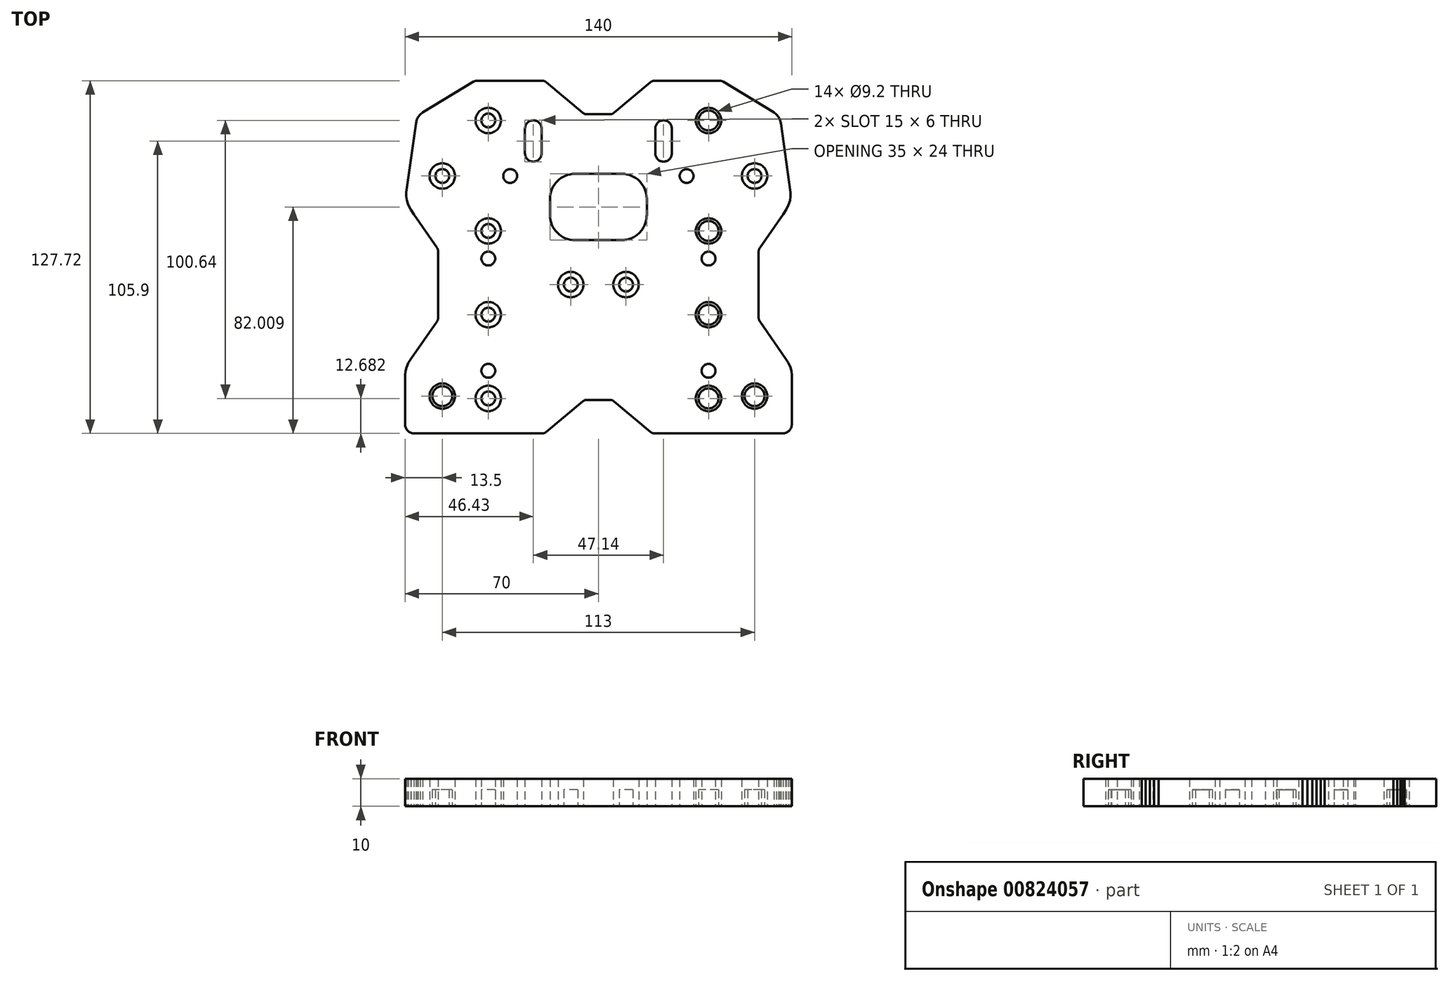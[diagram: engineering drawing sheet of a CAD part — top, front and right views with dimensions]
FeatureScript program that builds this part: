
annotation { "Feature Type Name" : "Feature", "Feature Type Description" : "" }
export const myFeature = defineFeature(function(context is Context, id is Id, definition is map)
    precondition{}
    {
        {
            var Q0;
            Q0=qCreatedBy(makeId("Top.planeOp"),FACE);
            var sketch = newSketch(context, id + "F0", { "sketchPlane" : qUnion([Q0])});
            skLineSegment(sketch, "E0", {"start": v(-63.59, 52.34) * mm, "end": v(-64.5, 51.65) * mm});
            skLineSegment(sketch, "E1", {"start": v(-64.5, 51.65) * mm, "end": v(-65.2, 50.76) * mm});
            skLineSegment(sketch, "E2", {"start": v(-65.2, 50.76) * mm, "end": v(-65.7, 49.68) * mm});
            skLineSegment(sketch, "E3", {"start": v(-65.7, 49.68) * mm, "end": v(-66.02, 48.35) * mm});
            skLineSegment(sketch, "E4", {"start": v(-63.59, 52.34) * mm, "end": v(-45.13, 63.52) * mm});
            skLineSegment(sketch, "E5", {"start": v(-70, -42.75) * mm, "end": v(-70, -60.5) * mm});
            skLineSegment(sketch, "E6", {"start": v(-69.52, 23.45) * mm, "end": v(-66.02, 48.35) * mm});
            skLineSegment(sketch, "E7", {"start": v(-70, -42.75) * mm, "end": v(-69.87, -41.37) * mm});
            skLineSegment(sketch, "E8", {"start": v(-69.87, -41.37) * mm, "end": v(-69.45, -39.88) * mm});
            skLineSegment(sketch, "E9", {"start": v(-69.45, -39.88) * mm, "end": v(-68.74, -38.32) * mm});
            skLineSegment(sketch, "E10", {"start": v(-68.74, -38.32) * mm, "end": v(-67.73, -36.7) * mm});
            skLineSegment(sketch, "E11", {"start": v(-66.64, -63.86) * mm, "end": v(-20.35, -63.86) * mm});
            skLineSegment(sketch, "E12", {"start": v(20.35, -63.86) * mm, "end": v(66.64, -63.86) * mm});
            skLineSegment(sketch, "E13", {"start": v(-58, -22) * mm, "end": v(-58, 2.08) * mm});
            skLineSegment(sketch, "E14", {"start": v(4.14, -51.7) * mm, "end": v(-4.14, -51.7) * mm});
            skLineSegment(sketch, "E15", {"start": v(-58.43, 3.42) * mm, "end": v(-66.79, 15.4) * mm});
            skLineSegment(sketch, "E16", {"start": v(-66.79, 15.4) * mm, "end": v(-67.92, 17.2) * mm});
            skLineSegment(sketch, "E17", {"start": v(-67.92, 17.2) * mm, "end": v(-68.77, 18.92) * mm});
            skLineSegment(sketch, "E18", {"start": v(-68.77, 18.92) * mm, "end": v(-69.32, 20.55) * mm});
            skLineSegment(sketch, "E19", {"start": v(-69.32, 20.55) * mm, "end": v(-69.57, 22.07) * mm});
            skLineSegment(sketch, "E20", {"start": v(-69.57, 22.07) * mm, "end": v(-69.52, 23.45) * mm});
            skLineSegment(sketch, "E21", {"start": v(-67.73, -36.7) * mm, "end": v(-58.43, -23.34) * mm});
            skLineSegment(sketch, "E22", {"start": v(5.66, 52.25) * mm, "end": v(18.84, 63.31) * mm});
            skLineSegment(sketch, "E23", {"start": v(18.84, -63.31) * mm, "end": v(5.66, -52.25) * mm});
            skLineSegment(sketch, "E24", {"start": v(-26.57, 46.54) * mm, "end": v(-26.57, 37.54) * mm});
            skLineSegment(sketch, "E25", {"start": v(-20.57, 37.54) * mm, "end": v(-20.57, 46.54) * mm});
            skLineSegment(sketch, "E26", {"start": v(-17.5, 21.1) * mm, "end": v(-17.5, 15.2) * mm});
            skLineSegment(sketch, "E27", {"start": v(-8.45, 6.15) * mm, "end": v(8.45, 6.15) * mm});
            skLineSegment(sketch, "E28", {"start": v(17.5, 15.2) * mm, "end": v(17.5, 21.1) * mm});
            skLineSegment(sketch, "E29", {"start": v(20.57, 46.54) * mm, "end": v(20.57, 37.54) * mm});
            skLineSegment(sketch, "E30", {"start": v(26.57, 37.54) * mm, "end": v(26.57, 46.54) * mm});
            skLineSegment(sketch, "E31", {"start": v(8.45, 30.15) * mm, "end": v(-8.45, 30.15) * mm});
            skLineSegment(sketch, "E32", {"start": v(-5.66, -52.25) * mm, "end": v(-18.84, -63.31) * mm});
            skLineSegment(sketch, "E33", {"start": v(-18.84, 63.31) * mm, "end": v(-5.66, 52.25) * mm});
            skLineSegment(sketch, "E34", {"start": v(58.43, -23.33) * mm, "end": v(67.73, -36.7) * mm});
            skLineSegment(sketch, "E35", {"start": v(66.78, 15.4) * mm, "end": v(58.43, 3.42) * mm});
            skLineSegment(sketch, "E36", {"start": v(-4.14, 51.7) * mm, "end": v(4.14, 51.7) * mm});
            skLineSegment(sketch, "E37", {"start": v(58, 2.08) * mm, "end": v(58, -22) * mm});
            skLineSegment(sketch, "E38", {"start": v(43.91, 63.86) * mm, "end": v(20.35, 63.86) * mm});
            skLineSegment(sketch, "E39", {"start": v(-20.35, 63.86) * mm, "end": v(-43.91, 63.86) * mm});
            skLineSegment(sketch, "E40", {"start": v(70, -42.75) * mm, "end": v(69.87, -41.37) * mm});
            skLineSegment(sketch, "E41", {"start": v(69.87, -41.37) * mm, "end": v(69.45, -39.88) * mm});
            skLineSegment(sketch, "E42", {"start": v(69.45, -39.88) * mm, "end": v(68.74, -38.32) * mm});
            skLineSegment(sketch, "E43", {"start": v(68.74, -38.32) * mm, "end": v(67.73, -36.7) * mm});
            skLineSegment(sketch, "E44", {"start": v(69.52, 23.45) * mm, "end": v(69.57, 22.07) * mm});
            skLineSegment(sketch, "E45", {"start": v(69.57, 22.07) * mm, "end": v(69.32, 20.55) * mm});
            skLineSegment(sketch, "E46", {"start": v(69.32, 20.55) * mm, "end": v(68.77, 18.92) * mm});
            skLineSegment(sketch, "E47", {"start": v(68.77, 18.92) * mm, "end": v(67.92, 17.2) * mm});
            skLineSegment(sketch, "E48", {"start": v(67.92, 17.2) * mm, "end": v(66.78, 15.4) * mm});
            skLineSegment(sketch, "E49", {"start": v(70, -60.5) * mm, "end": v(70, -42.75) * mm});
            skLineSegment(sketch, "E50", {"start": v(66.02, 48.35) * mm, "end": v(65.7, 49.7) * mm});
            skLineSegment(sketch, "E51", {"start": v(65.7, 49.7) * mm, "end": v(65.17, 50.8) * mm});
            skLineSegment(sketch, "E52", {"start": v(65.17, 50.8) * mm, "end": v(64.47, 51.66) * mm});
            skLineSegment(sketch, "E53", {"start": v(64.47, 51.66) * mm, "end": v(63.59, 52.34) * mm});
            skLineSegment(sketch, "E54", {"start": v(66.02, 48.35) * mm, "end": v(69.52, 23.45) * mm});
            skLineSegment(sketch, "E55", {"start": v(45.13, 63.52) * mm, "end": v(63.59, 52.34) * mm});
            skCircle(sketch, "E56", {"center": v(-56.5, -50.34) * mm, "radius": 3.6 * mm});
            skArc(sketch, "E57", {"start": v(-70, -60.5) * mm, "mid": v(-69.02, -62.88) * mm, "end": v(-66.64, -63.86) * mm});
            skCircle(sketch, "E58", {"center": v(-10, -9.96) * mm, "radius": 2.5 * mm});
            skCircle(sketch, "E59", {"center": v(-39.85, -51.18) * mm, "radius": 2.5 * mm});
            skCircle(sketch, "E60", {"center": v(-39.85, -41.18) * mm, "radius": 2.5 * mm});
            skCircle(sketch, "E61", {"center": v(-39.85, -20.86) * mm, "radius": 2.5 * mm});
            skCircle(sketch, "E62", {"center": v(-39.85, -0.54) * mm, "radius": 2.5 * mm});
            skArc(sketch, "E63", {"start": v(-4.14, -51.7) * mm, "mid": v(-4.95, -51.84) * mm, "end": v(-5.66, -52.25) * mm});
            skArc(sketch, "E64", {"start": v(-58.43, -23.34) * mm, "mid": v(-58.11, -22.7) * mm, "end": v(-58, -22) * mm});
            skArc(sketch, "E65", {"start": v(-20.35, -63.86) * mm, "mid": v(-19.54, -63.72) * mm, "end": v(-18.84, -63.31) * mm});
            skArc(sketch, "E66", {"start": v(-8.45, 30.15) * mm, "mid": v(-14.85, 27.5) * mm, "end": v(-17.5, 21.1) * mm});
            skArc(sketch, "E67", {"start": v(-17.5, 15.2) * mm, "mid": v(-14.85, 8.8) * mm, "end": v(-8.45, 6.15) * mm});
            skArc(sketch, "E68", {"start": v(-20.57, 46.54) * mm, "mid": v(-23.57, 49.54) * mm, "end": v(-26.57, 46.54) * mm});
            skArc(sketch, "E69", {"start": v(-26.57, 37.54) * mm, "mid": v(-23.57, 34.54) * mm, "end": v(-20.57, 37.54) * mm});
            skCircle(sketch, "E70", {"center": v(-31.93, 29.36) * mm, "radius": 2.5 * mm});
            skCircle(sketch, "E71", {"center": v(-39.85, 9.46) * mm, "radius": 2.5 * mm});
            skCircle(sketch, "E72", {"center": v(-39.85, 49.46) * mm, "radius": 2.5 * mm});
            skCircle(sketch, "E73", {"center": v(-56.5, 29.36) * mm, "radius": 2.5 * mm});
            skArc(sketch, "E74", {"start": v(-58, 2.08) * mm, "mid": v(-58.11, 2.78) * mm, "end": v(-58.43, 3.42) * mm});
            skArc(sketch, "E75", {"start": v(-5.66, 52.25) * mm, "mid": v(-4.95, 51.84) * mm, "end": v(-4.14, 51.7) * mm});
            skArc(sketch, "E76", {"start": v(-18.84, 63.31) * mm, "mid": v(-19.54, 63.72) * mm, "end": v(-20.35, 63.86) * mm});
            skArc(sketch, "E77", {"start": v(-43.91, 63.86) * mm, "mid": v(-44.54, 63.77) * mm, "end": v(-45.13, 63.52) * mm});
            skCircle(sketch, "E78", {"center": v(39.85, -51.18) * mm, "radius": 3.6 * mm});
            skCircle(sketch, "E79", {"center": v(39.85, -20.86) * mm, "radius": 3.6 * mm});
            skCircle(sketch, "E80", {"center": v(56.5, -50.34) * mm, "radius": 3.6 * mm});
            skArc(sketch, "E81", {"start": v(66.64, -63.86) * mm, "mid": v(69.02, -62.88) * mm, "end": v(70, -60.5) * mm});
            skCircle(sketch, "E82", {"center": v(10, -9.96) * mm, "radius": 2.5 * mm});
            skCircle(sketch, "E83", {"center": v(39.85, -41.18) * mm, "radius": 2.5 * mm});
            skCircle(sketch, "E84", {"center": v(39.85, -0.54) * mm, "radius": 2.5 * mm});
            skArc(sketch, "E85", {"start": v(5.66, -52.25) * mm, "mid": v(4.95, -51.84) * mm, "end": v(4.14, -51.7) * mm});
            skArc(sketch, "E86", {"start": v(58, -22) * mm, "mid": v(58.12, -22.7) * mm, "end": v(58.43, -23.33) * mm});
            skArc(sketch, "E87", {"start": v(18.84, -63.31) * mm, "mid": v(19.54, -63.72) * mm, "end": v(20.35, -63.86) * mm});
            skArc(sketch, "E88", {"start": v(8.45, 6.15) * mm, "mid": v(14.85, 8.8) * mm, "end": v(17.5, 15.2) * mm});
            skArc(sketch, "E89", {"start": v(17.5, 21.1) * mm, "mid": v(14.85, 27.5) * mm, "end": v(8.45, 30.15) * mm});
            skCircle(sketch, "E90", {"center": v(39.85, 9.46) * mm, "radius": 3.6 * mm});
            skCircle(sketch, "E91", {"center": v(39.85, 49.46) * mm, "radius": 3.6 * mm});
            skArc(sketch, "E92", {"start": v(26.57, 46.54) * mm, "mid": v(23.57, 49.54) * mm, "end": v(20.57, 46.54) * mm});
            skArc(sketch, "E93", {"start": v(20.57, 37.54) * mm, "mid": v(23.57, 34.54) * mm, "end": v(26.57, 37.54) * mm});
            skCircle(sketch, "E94", {"center": v(31.92, 29.36) * mm, "radius": 2.5 * mm});
            skCircle(sketch, "E95", {"center": v(56.5, 29.36) * mm, "radius": 2.5 * mm});
            skArc(sketch, "E96", {"start": v(58.43, 3.42) * mm, "mid": v(58.12, 2.78) * mm, "end": v(58, 2.08) * mm});
            skArc(sketch, "E97", {"start": v(4.14, 51.7) * mm, "mid": v(4.95, 51.84) * mm, "end": v(5.66, 52.25) * mm});
            skArc(sketch, "E98", {"start": v(20.35, 63.86) * mm, "mid": v(19.54, 63.72) * mm, "end": v(18.84, 63.31) * mm});
            skArc(sketch, "E99", {"start": v(45.13, 63.52) * mm, "mid": v(44.54, 63.77) * mm, "end": v(43.91, 63.86) * mm});
            skCircle(sketch, "E100.0", {"center": v(39.85, 9.46) * mm, "radius": 4.6 * mm});
            skCircle(sketch, "E101.0", {"center": v(39.85, -20.86) * mm, "radius": 4.6 * mm});
            skCircle(sketch, "E102.0", {"center": v(39.85, -51.18) * mm, "radius": 4.6 * mm});
            skCircle(sketch, "E103.0", {"center": v(-39.85, 9.46) * mm, "radius": 4.6 * mm});
            skCircle(sketch, "E104.0", {"center": v(-39.85, -20.86) * mm, "radius": 4.6 * mm});
            skCircle(sketch, "E105.0", {"center": v(-39.85, -51.18) * mm, "radius": 4.6 * mm});
            skCircle(sketch, "E106.0", {"center": v(-39.85, 49.46) * mm, "radius": 4.6 * mm});
            skCircle(sketch, "E107.0", {"center": v(39.85, 49.46) * mm, "radius": 4.6 * mm});
            skCircle(sketch, "E108.0", {"center": v(-10, -9.96) * mm, "radius": 4.6 * mm});
            skCircle(sketch, "E109.0", {"center": v(10, -9.96) * mm, "radius": 4.6 * mm});
            skCircle(sketch, "E110.0", {"center": v(56.5, -50.34) * mm, "radius": 4.6 * mm});
            skCircle(sketch, "E111.0", {"center": v(-56.5, -50.34) * mm, "radius": 4.6 * mm});
            skCircle(sketch, "E112.0", {"center": v(-56.5, 29.36) * mm, "radius": 4.6 * mm});
            skCircle(sketch, "E113.0", {"center": v(56.5, 29.36) * mm, "radius": 4.6 * mm});
            skSolve(sketch);
        }
        {
            var Q0;
            Q0=makeQuery(id+"F0.imprint","IMPRINT",FACE,{"disambiguationData":[TD([[makeQuery(id+"F0.imprint","IMPRINT",EDGE,{"derivedFrom":sQuery(id+"F0.wireOp",EDGE,"E0")}),1.0]])]});
            extrude(context, id + "F1", {"entities" : qUnion([Q0]), "depth" : 10 * mm, "offsetDistance" : 25 * mm});
        }
        {
            var Q0;
            Q0=makeQuery(id+"F0.imprint","IMPRINT",FACE,{"disambiguationData":[TD([[makeQuery(id+"F0.imprint","IMPRINT",EDGE,{"derivedFrom":sQuery(id+"F0.wireOp",EDGE,"E71")}),1.0]])]});
            var Q1;
            Q1=makeQuery(id+"F0.imprint","IMPRINT",FACE,{"disambiguationData":[TD([[makeQuery(id+"F0.imprint","IMPRINT",EDGE,{"derivedFrom":sQuery(id+"F0.wireOp",EDGE,"E61")}),1.0]])]});
            var Q2;
            Q2=makeQuery(id+"F0.imprint","IMPRINT",FACE,{"disambiguationData":[TD([[makeQuery(id+"F0.imprint","IMPRINT",EDGE,{"derivedFrom":sQuery(id+"F0.wireOp",EDGE,"E59")}),1.0]])]});
            var Q3;
            Q3=makeQuery(id+"F0.imprint","IMPRINT",FACE,{"disambiguationData":[TD([[makeQuery(id+"F0.imprint","IMPRINT",EDGE,{"derivedFrom":sQuery(id+"F0.wireOp",EDGE,"E79")}),1.0]])]});
            var Q4;
            Q4=makeQuery(id+"F0.imprint","IMPRINT",FACE,{"disambiguationData":[TD([[makeQuery(id+"F0.imprint","IMPRINT",EDGE,{"derivedFrom":sQuery(id+"F0.wireOp",EDGE,"E78")}),1.0]])]});
            var Q5;
            Q5=makeQuery(id+"F0.imprint","IMPRINT",FACE,{"disambiguationData":[TD([[makeQuery(id+"F0.imprint","IMPRINT",EDGE,{"derivedFrom":sQuery(id+"F0.wireOp",EDGE,"E90")}),1.0]])]});
            var Q6;
            Q6=makeQuery(id+"F0.imprint","IMPRINT",FACE,{"disambiguationData":[TD([[makeQuery(id+"F0.imprint","IMPRINT",EDGE,{"derivedFrom":sQuery(id+"F0.wireOp",EDGE,"E72")}),1.0]])]});
            var Q7;
            Q7=makeQuery(id+"F0.imprint","IMPRINT",FACE,{"disambiguationData":[TD([[makeQuery(id+"F0.imprint","IMPRINT",EDGE,{"derivedFrom":sQuery(id+"F0.wireOp",EDGE,"E91")}),1.0]])]});
            var Q8;
            Q8=makeQuery(id+"F0.imprint","IMPRINT",FACE,{"disambiguationData":[TD([[makeQuery(id+"F0.imprint","IMPRINT",EDGE,{"derivedFrom":sQuery(id+"F0.wireOp",EDGE,"E58")}),1.0]])]});
            var Q9;
            Q9=makeQuery(id+"F0.imprint","IMPRINT",FACE,{"disambiguationData":[TD([[makeQuery(id+"F0.imprint","IMPRINT",EDGE,{"derivedFrom":sQuery(id+"F0.wireOp",EDGE,"E82")}),1.0]])]});
            var Q10;
            Q10=makeQuery(id+"F0.imprint","IMPRINT",FACE,{"disambiguationData":[TD([[makeQuery(id+"F0.imprint","IMPRINT",EDGE,{"derivedFrom":sQuery(id+"F0.wireOp",EDGE,"E56")}),1.0]])]});
            var Q11;
            Q11=makeQuery(id+"F0.imprint","IMPRINT",FACE,{"disambiguationData":[TD([[makeQuery(id+"F0.imprint","IMPRINT",EDGE,{"derivedFrom":sQuery(id+"F0.wireOp",EDGE,"E95")}),1.0]])]});
            var Q12;
            Q12=makeQuery(id+"F0.imprint","IMPRINT",FACE,{"disambiguationData":[TD([[makeQuery(id+"F0.imprint","IMPRINT",EDGE,{"derivedFrom":sQuery(id+"F0.wireOp",EDGE,"E80")}),1.0]])]});
            var Q13;
            Q13=makeQuery(id+"F0.imprint","IMPRINT",FACE,{"disambiguationData":[TD([[makeQuery(id+"F0.imprint","IMPRINT",EDGE,{"derivedFrom":sQuery(id+"F0.wireOp",EDGE,"E73")}),1.0]])]});
            var Q14;
            Q14=makeQuery(id+"F1.opExtrude","CAP_FACE",FACE,{"disambiguationData":[OSD([sQuery(id+"F0.wireOp",EDGE,"E0"),sQuery(id+"F0.wireOp",EDGE,"E1"),sQuery(id+"F0.wireOp",EDGE,"E2"),sQuery(id+"F0.wireOp",EDGE,"E3"),sQuery(id+"F0.wireOp",EDGE,"E4"),sQuery(id+"F0.wireOp",EDGE,"E5"),sQuery(id+"F0.wireOp",EDGE,"E6"),sQuery(id+"F0.wireOp",EDGE,"E7"),sQuery(id+"F0.wireOp",EDGE,"E8"),sQuery(id+"F0.wireOp",EDGE,"E9"),sQuery(id+"F0.wireOp",EDGE,"E10"),sQuery(id+"F0.wireOp",EDGE,"E11"),sQuery(id+"F0.wireOp",EDGE,"E12"),sQuery(id+"F0.wireOp",EDGE,"E13"),sQuery(id+"F0.wireOp",EDGE,"E14"),sQuery(id+"F0.wireOp",EDGE,"E15"),sQuery(id+"F0.wireOp",EDGE,"E16"),sQuery(id+"F0.wireOp",EDGE,"E17"),sQuery(id+"F0.wireOp",EDGE,"E18"),sQuery(id+"F0.wireOp",EDGE,"E19"),sQuery(id+"F0.wireOp",EDGE,"E20"),sQuery(id+"F0.wireOp",EDGE,"E21"),sQuery(id+"F0.wireOp",EDGE,"E22"),sQuery(id+"F0.wireOp",EDGE,"E23"),sQuery(id+"F0.wireOp",EDGE,"E24"),sQuery(id+"F0.wireOp",EDGE,"E25"),sQuery(id+"F0.wireOp",EDGE,"E26"),sQuery(id+"F0.wireOp",EDGE,"E27"),sQuery(id+"F0.wireOp",EDGE,"E28"),sQuery(id+"F0.wireOp",EDGE,"E29"),sQuery(id+"F0.wireOp",EDGE,"E30"),sQuery(id+"F0.wireOp",EDGE,"E31"),sQuery(id+"F0.wireOp",EDGE,"E32"),sQuery(id+"F0.wireOp",EDGE,"E33"),sQuery(id+"F0.wireOp",EDGE,"E34"),sQuery(id+"F0.wireOp",EDGE,"E35"),sQuery(id+"F0.wireOp",EDGE,"E36"),sQuery(id+"F0.wireOp",EDGE,"E37"),sQuery(id+"F0.wireOp",EDGE,"E38"),sQuery(id+"F0.wireOp",EDGE,"E39"),sQuery(id+"F0.wireOp",EDGE,"E40"),sQuery(id+"F0.wireOp",EDGE,"E41"),sQuery(id+"F0.wireOp",EDGE,"E42"),sQuery(id+"F0.wireOp",EDGE,"E43"),sQuery(id+"F0.wireOp",EDGE,"E44"),sQuery(id+"F0.wireOp",EDGE,"E45"),sQuery(id+"F0.wireOp",EDGE,"E46"),sQuery(id+"F0.wireOp",EDGE,"E47"),sQuery(id+"F0.wireOp",EDGE,"E48"),sQuery(id+"F0.wireOp",EDGE,"E49"),sQuery(id+"F0.wireOp",EDGE,"E50"),sQuery(id+"F0.wireOp",EDGE,"E51"),sQuery(id+"F0.wireOp",EDGE,"E52"),sQuery(id+"F0.wireOp",EDGE,"E53"),sQuery(id+"F0.wireOp",EDGE,"E54"),sQuery(id+"F0.wireOp",EDGE,"E55"),sQuery(id+"F0.wireOp",EDGE,"E56"),sQuery(id+"F0.wireOp",EDGE,"E57"),sQuery(id+"F0.wireOp",EDGE,"E58"),sQuery(id+"F0.wireOp",EDGE,"E59"),sQuery(id+"F0.wireOp",EDGE,"E60"),sQuery(id+"F0.wireOp",EDGE,"E61"),sQuery(id+"F0.wireOp",EDGE,"E62"),sQuery(id+"F0.wireOp",EDGE,"E63"),sQuery(id+"F0.wireOp",EDGE,"E64"),sQuery(id+"F0.wireOp",EDGE,"E65"),sQuery(id+"F0.wireOp",EDGE,"E66"),sQuery(id+"F0.wireOp",EDGE,"E67"),sQuery(id+"F0.wireOp",EDGE,"E68"),sQuery(id+"F0.wireOp",EDGE,"E69"),sQuery(id+"F0.wireOp",EDGE,"E70"),sQuery(id+"F0.wireOp",EDGE,"E71"),sQuery(id+"F0.wireOp",EDGE,"E72"),sQuery(id+"F0.wireOp",EDGE,"E73"),sQuery(id+"F0.wireOp",EDGE,"E74"),sQuery(id+"F0.wireOp",EDGE,"E75"),sQuery(id+"F0.wireOp",EDGE,"E76"),sQuery(id+"F0.wireOp",EDGE,"E77"),sQuery(id+"F0.wireOp",EDGE,"E78"),sQuery(id+"F0.wireOp",EDGE,"E79"),sQuery(id+"F0.wireOp",EDGE,"E80"),sQuery(id+"F0.wireOp",EDGE,"E81"),sQuery(id+"F0.wireOp",EDGE,"E82"),sQuery(id+"F0.wireOp",EDGE,"E83"),sQuery(id+"F0.wireOp",EDGE,"E84"),sQuery(id+"F0.wireOp",EDGE,"E85"),sQuery(id+"F0.wireOp",EDGE,"E86"),sQuery(id+"F0.wireOp",EDGE,"E87"),sQuery(id+"F0.wireOp",EDGE,"E88"),sQuery(id+"F0.wireOp",EDGE,"E89"),sQuery(id+"F0.wireOp",EDGE,"E90"),sQuery(id+"F0.wireOp",EDGE,"E91"),sQuery(id+"F0.wireOp",EDGE,"E92"),sQuery(id+"F0.wireOp",EDGE,"E93"),sQuery(id+"F0.wireOp",EDGE,"E94"),sQuery(id+"F0.wireOp",EDGE,"E95"),sQuery(id+"F0.wireOp",EDGE,"E96"),sQuery(id+"F0.wireOp",EDGE,"E97"),sQuery(id+"F0.wireOp",EDGE,"E98"),sQuery(id+"F0.wireOp",EDGE,"E99")])],"isStart":false});
            extrude(context, id + "F2", {"entities" : qUnion([Q0, Q1, Q2, Q3, Q4, Q5, Q6, Q7, Q8, Q9, Q10, Q11, Q12, Q13]), "operationType" : NewBodyOperationType.ADD, "depth" : 6 * mm, "endBoundEntityFace" : qUnion([Q14]), "hasOffset" : true, "offsetDistance" : 6 * mm});
        }
    });
